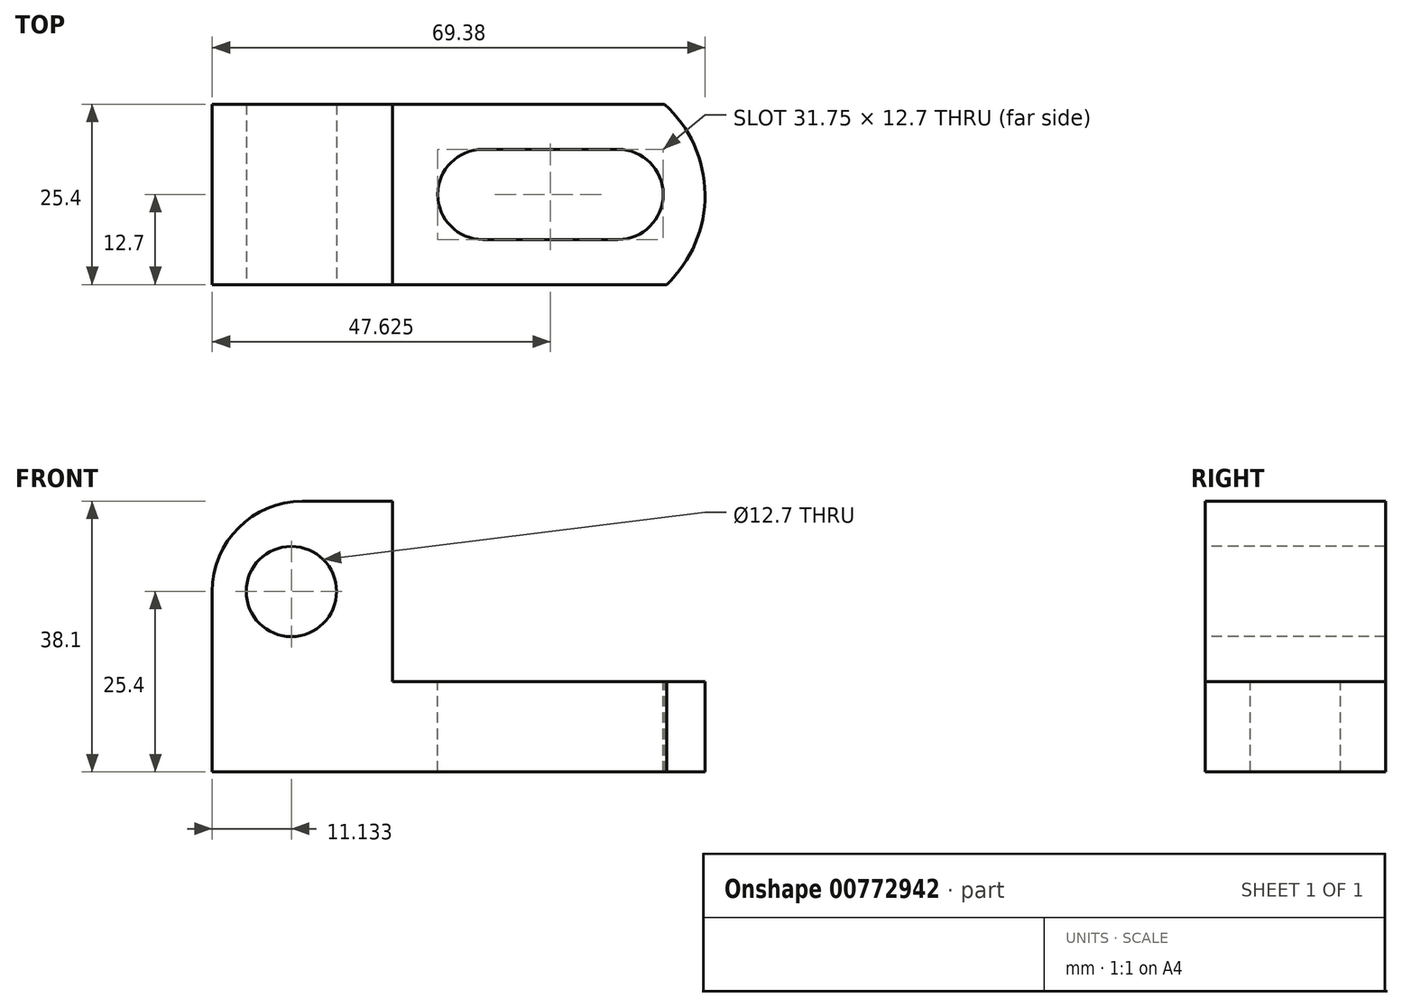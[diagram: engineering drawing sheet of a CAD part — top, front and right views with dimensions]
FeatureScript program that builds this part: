
annotation { "Feature Type Name" : "Feature", "Feature Type Description" : "" }
export const myFeature = defineFeature(function(context is Context, id is Id, definition is map)
    precondition{}
    {
        {
            var Q0;
            Q0=qCreatedBy(makeId("Front.planeOp"),FACE);
            var sketch = newSketch(context, id + "F0", { "sketchPlane" : qUnion([Q0])});
            skLineSegment(sketch, "E0", {"start": v(0, 0) * mm, "end": v(69.85, 0) * mm});
            skLineSegment(sketch, "E1", {"start": v(69.85, 0) * mm, "end": v(69.85, 38.1) * mm});
            skLineSegment(sketch, "E2", {"start": v(69.85, 38.1) * mm, "end": v(0, 38.1) * mm});
            skLineSegment(sketch, "E3", {"start": v(0, 38.1) * mm, "end": v(0, 0) * mm});
            skSolve(sketch);
        }
        {
            var Q0;
            Q0=makeQuery(id+"F0.imprint","IMPRINT",FACE,{"disambiguationData":[TD([[makeQuery(id+"F0.imprint","IMPRINT",EDGE,{"derivedFrom":sQuery(id+"F0.wireOp",EDGE,"E0")}),1.0]])]});
            extrude(context, id + "F1", {"entities" : qUnion([Q0]), "depth" : 25.4 * mm, "offsetDistance" : 25.4 * mm});
        }
        {
            var Q0;
            Q0=makeQuery(id+"F1.opExtrude","CAP_FACE",FACE,{"disambiguationData":[OSD([sQuery(id+"F0.wireOp",EDGE,"E0"),sQuery(id+"F0.wireOp",EDGE,"E1"),sQuery(id+"F0.wireOp",EDGE,"E2"),sQuery(id+"F0.wireOp",EDGE,"E3")])],"isStart":false});
            var sketch = newSketch(context, id + "F2", { "sketchPlane" : qUnion([Q0])});
            skLineSegment(sketch, "E4", {"start": v(25.4, 38.1) * mm, "end": v(25.4, 12.7) * mm});
            skLineSegment(sketch, "E5", {"start": v(25.4, 12.7) * mm, "end": v(69.85, 12.7) * mm});
            skLineSegment(sketch, "E6", {"start": v(69.85, 12.7) * mm, "end": v(69.85, 38.1) * mm});
            skLineSegment(sketch, "E7", {"start": v(69.85, 38.1) * mm, "end": v(25.4, 38.1) * mm});
            skSolve(sketch);
        }
        {
            var Q0;
            Q0=makeQuery(id+"F2.imprint","IMPRINT",FACE,{"disambiguationData":[TD([[makeQuery(id+"F2.imprint","IMPRINT",EDGE,{"derivedFrom":sQuery(id+"F2.wireOp",EDGE,"E4")}),1.0]])]});
            extrude(context, id + "F3", {"entities" : qUnion([Q0]), "operationType" : NewBodyOperationType.REMOVE, "oppositeDirection" : true, "depth" : 25.4 * mm, "offsetDistance" : 25.4 * mm});
        }
        {
            var Q0;
            Q0=makeQuery(id+"F3.boolean.opBoolean","COPY",EDGE,{"derivedFrom":makeQuery(id+"F3.opExtrude","SWEPT_EDGE",EDGE,{"disambiguationData":[OSD([sQuery(id+"F0.wireOp",EDGE,"E2"),sQuery(id+"F2.wireOp",EDGE,"E4"),sQuery(id+"F2.wireOp",EDGE,"E7")])]})});
            var Q1;
            Q1=makeQuery(id+"F1.opExtrude","SWEPT_EDGE",EDGE,{"disambiguationData":[OSD([sQuery(id+"F0.wireOp",EDGE,"E2"),sQuery(id+"F0.wireOp",EDGE,"E3")])]});
            fillet(context, id + "F4", {"entities" : qUnion([Q0, Q1]), "radius" : 12.7 * mm, "tangentPropagation" : true, "allowEdgeOverflow" : false});
        }
        {
            var Q0;
            Q0=makeQuery(id+"F1.opExtrude","CAP_FACE",FACE,{"disambiguationData":[OSD([sQuery(id+"F0.wireOp",EDGE,"E0"),sQuery(id+"F0.wireOp",EDGE,"E1"),sQuery(id+"F0.wireOp",EDGE,"E2"),sQuery(id+"F0.wireOp",EDGE,"E3")])],"isStart":false});
            var sketch = newSketch(context, id + "F5", { "sketchPlane" : qUnion([Q0])});
            skCircle(sketch, "E8", {"center": v(11.13, 25.4) * mm, "radius": 6.35 * mm});
            skSolve(sketch);
        }
        {
            var Q0;
            Q0=makeQuery(id+"F5.imprint","IMPRINT",FACE,{"disambiguationData":[TD([[makeQuery(id+"F5.imprint","IMPRINT",EDGE,{"derivedFrom":sQuery(id+"F5.wireOp",EDGE,"E8")}),1.0]])]});
            extrude(context, id + "F6", {"entities" : qUnion([Q0]), "operationType" : NewBodyOperationType.REMOVE, "oppositeDirection" : true, "depth" : 25.4 * mm, "offsetDistance" : 25.4 * mm});
        }
        {
            var Q0;
            Q0=makeQuery(id+"F3.boolean.opBoolean","COPY",FACE,{"derivedFrom":makeQuery(id+"F3.opExtrude","SWEPT_FACE",FACE,{"disambiguationData":[OSD([sQuery(id+"F2.wireOp",EDGE,"E5")])]})});
            var sketch = newSketch(context, id + "F7", { "sketchPlane" : qUnion([Q0])});
            skCircle(sketch, "E9", {"center": v(38.1, -12.7) * mm, "radius": 6.35 * mm});
            skCircle(sketch, "E10", {"center": v(57.15, -12.7) * mm, "radius": 6.35 * mm});
            skLineSegment(sketch, "E11", {"start": v(38.1, -19.05) * mm, "end": v(57.15, -19.05) * mm});
            skLineSegment(sketch, "E12", {"start": v(38.1, -6.35) * mm, "end": v(57.15, -6.35) * mm});
            skSolve(sketch);
        }
        {
            var Q0;
            {var subQ0=sQuery(id+"F7.wireOp",EDGE,"E9");var subQ1=makeQuery(id+"F7.imprint","INTERSECT",VERTEX,{"derivedFrom":[subQ0,sQuery(id+"F7.wireOp",EDGE,"E11")]});Q0=makeQuery(id+"F7.imprint","IMPRINT",FACE,{"disambiguationData":[TD([[makeQuery(id+"F7.imprint","IMPRINT",EDGE,{"disambiguationData":[TD([[subQ1,1.0]])],"derivedFrom":subQ0}),1.0]])]});}
            var Q1;
            {var subQ0=sQuery(id+"F7.wireOp",EDGE,"E11");Q1=makeQuery(id+"F7.imprint","IMPRINT",FACE,{"disambiguationData":[TD([[makeQuery(id+"F7.imprint","IMPRINT",EDGE,{"derivedFrom":subQ0}),1.0]])]});}
            var Q2;
            {var subQ0=sQuery(id+"F7.wireOp",EDGE,"E10");var subQ1=makeQuery(id+"F7.imprint","INTERSECT",VERTEX,{"derivedFrom":[subQ0,sQuery(id+"F7.wireOp",EDGE,"E11")]});Q2=makeQuery(id+"F7.imprint","IMPRINT",FACE,{"disambiguationData":[TD([[makeQuery(id+"F7.imprint","IMPRINT",EDGE,{"disambiguationData":[TD([[subQ1,1.0]])],"derivedFrom":subQ0}),1.0]])]});}
            extrude(context, id + "F8", {"entities" : qUnion([Q0, Q1, Q2]), "operationType" : NewBodyOperationType.REMOVE, "oppositeDirection" : true, "depth" : 50.8 * mm, "offsetDistance" : 25.4 * mm});
        }
        {
            var Q0;
            Q0=makeQuery(id+"F3.boolean.opBoolean","COPY",FACE,{"derivedFrom":makeQuery(id+"F3.opExtrude","SWEPT_FACE",FACE,{"disambiguationData":[OSD([sQuery(id+"F2.wireOp",EDGE,"E5")])]})});
            var sketch = newSketch(context, id + "F9", { "sketchPlane" : qUnion([Q0])});
            skArc(sketch, "E13", {"start": v(63.98, -25.4) * mm, "mid": v(69.38, -12.64) * mm, "end": v(63.7, 0) * mm});
            skSolve(sketch);
        }
        {
            var Q0;
            {var subQ0=sQuery(id+"F9.wireOp",EDGE,"E13");Q0=makeQuery(id+"F9.imprint","IMPRINT",FACE,{"disambiguationData":[TD([[makeQuery(id+"F9.imprint","IMPRINT",EDGE,{"derivedFrom":subQ0}),-1.0]])]});}
            extrude(context, id + "F10", {"entities" : qUnion([Q0]), "operationType" : NewBodyOperationType.REMOVE, "oppositeDirection" : true, "depth" : 50.8 * mm, "offsetDistance" : 25.4 * mm});
        }
    });
